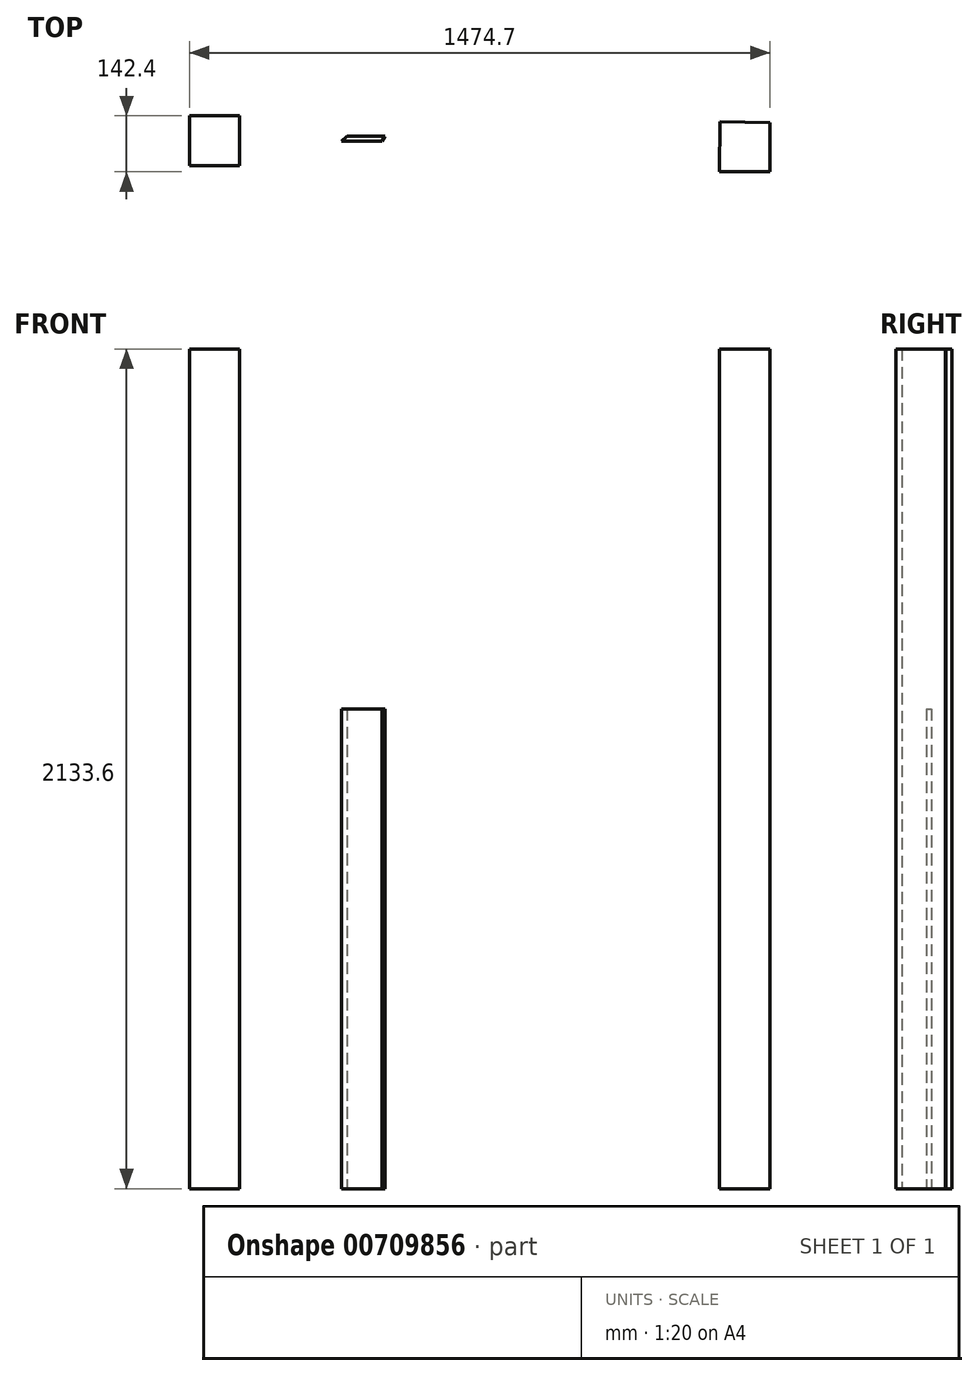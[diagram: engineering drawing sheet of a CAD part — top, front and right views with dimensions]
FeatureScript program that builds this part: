
annotation { "Feature Type Name" : "Feature", "Feature Type Description" : "" }
export const myFeature = defineFeature(function(context is Context, id is Id, definition is map)
    precondition{}
    {
        {
            var Q0;
            Q0=qCreatedBy(makeId("Top.planeOp"),FACE);
            var sketch = newSketch(context, id + "F0", { "sketchPlane" : qUnion([Q0])});
            skLineSegment(sketch, "E0", {"start": v(-53.3, 0) * mm, "end": v(-53.3, 127) * mm});
            skLineSegment(sketch, "E1", {"start": v(-53.3, 127) * mm, "end": v(73.7, 127) * mm});
            skLineSegment(sketch, "E2", {"start": v(73.7, 127) * mm, "end": v(73.7, 0) * mm});
            skLineSegment(sketch, "E3", {"start": v(73.7, 0) * mm, "end": v(-53.3, 0) * mm});
            skLineSegment(sketch, "E4", {"start": v(1292.8, -15.4) * mm, "end": v(1294.4, 111.59) * mm});
            skLineSegment(sketch, "E5", {"start": v(1294.4, 111.59) * mm, "end": v(1421.39, 109.98) * mm});
            skLineSegment(sketch, "E6", {"start": v(1421.39, 109.98) * mm, "end": v(1421.39, -15.4) * mm});
            skLineSegment(sketch, "E7", {"start": v(1421.39, -15.4) * mm, "end": v(1292.8, -15.4) * mm});
            skSolve(sketch);
        }
        {
            var Q0;
            Q0=makeQuery(id+"F0.imprint","IMPRINT",FACE,{"disambiguationData":[TD([[makeQuery(id+"F0.imprint","IMPRINT",EDGE,{"derivedFrom":sQuery(id+"F0.wireOp",EDGE,"E0")}),-1.0]])]});
            var Q1;
            Q1=makeQuery(id+"F0.imprint","IMPRINT",FACE,{"disambiguationData":[TD([[makeQuery(id+"F0.imprint","IMPRINT",EDGE,{"derivedFrom":sQuery(id+"F0.wireOp",EDGE,"E4")}),-1.0]])]});
            extrude(context, id + "F1", {"entities" : qUnion([Q0, Q1]), "depth" : 2133.6 * mm, "offsetDistance" : 25.4 * mm});
        }
        {
            var Q0;
            Q0=qCreatedBy(makeId("Top.planeOp"),FACE);
            var sketch = newSketch(context, id + "F2", { "sketchPlane" : qUnion([Q0])});
            skLineSegment(sketch, "E8", {"start": v(341.14, 62.05) * mm, "end": v(435.67, 62.05) * mm});
            skLineSegment(sketch, "E9.0", {"start": v(346.77, 74.75) * mm, "end": v(435.67, 74.75) * mm});
            skLineSegment(sketch, "E10", {"start": v(435.67, 74.75) * mm, "end": v(443.67, 74.75) * mm});
            skLineSegment(sketch, "E11", {"start": v(341.14, 62.05) * mm, "end": v(333.14, 62.05) * mm});
            skLineSegment(sketch, "E12", {"start": v(333.14, 62.05) * mm, "end": v(346.77, 74.75) * mm});
            skLineSegment(sketch, "E13", {"start": v(435.67, 62.05) * mm, "end": v(443.67, 74.75) * mm});
            skSolve(sketch);
        }
        {
            var Q0;
            Q0=makeQuery(id+"F2.imprint","IMPRINT",FACE,{"disambiguationData":[TD([[makeQuery(id+"F2.imprint","IMPRINT",EDGE,{"derivedFrom":sQuery(id+"F2.wireOp",EDGE,"E8")}),1.0]])]});
            extrude(context, id + "F3", {"entities" : qUnion([Q0]), "depth" : 1219.2 * mm, "offsetDistance" : 25.4 * mm});
        }
    });
